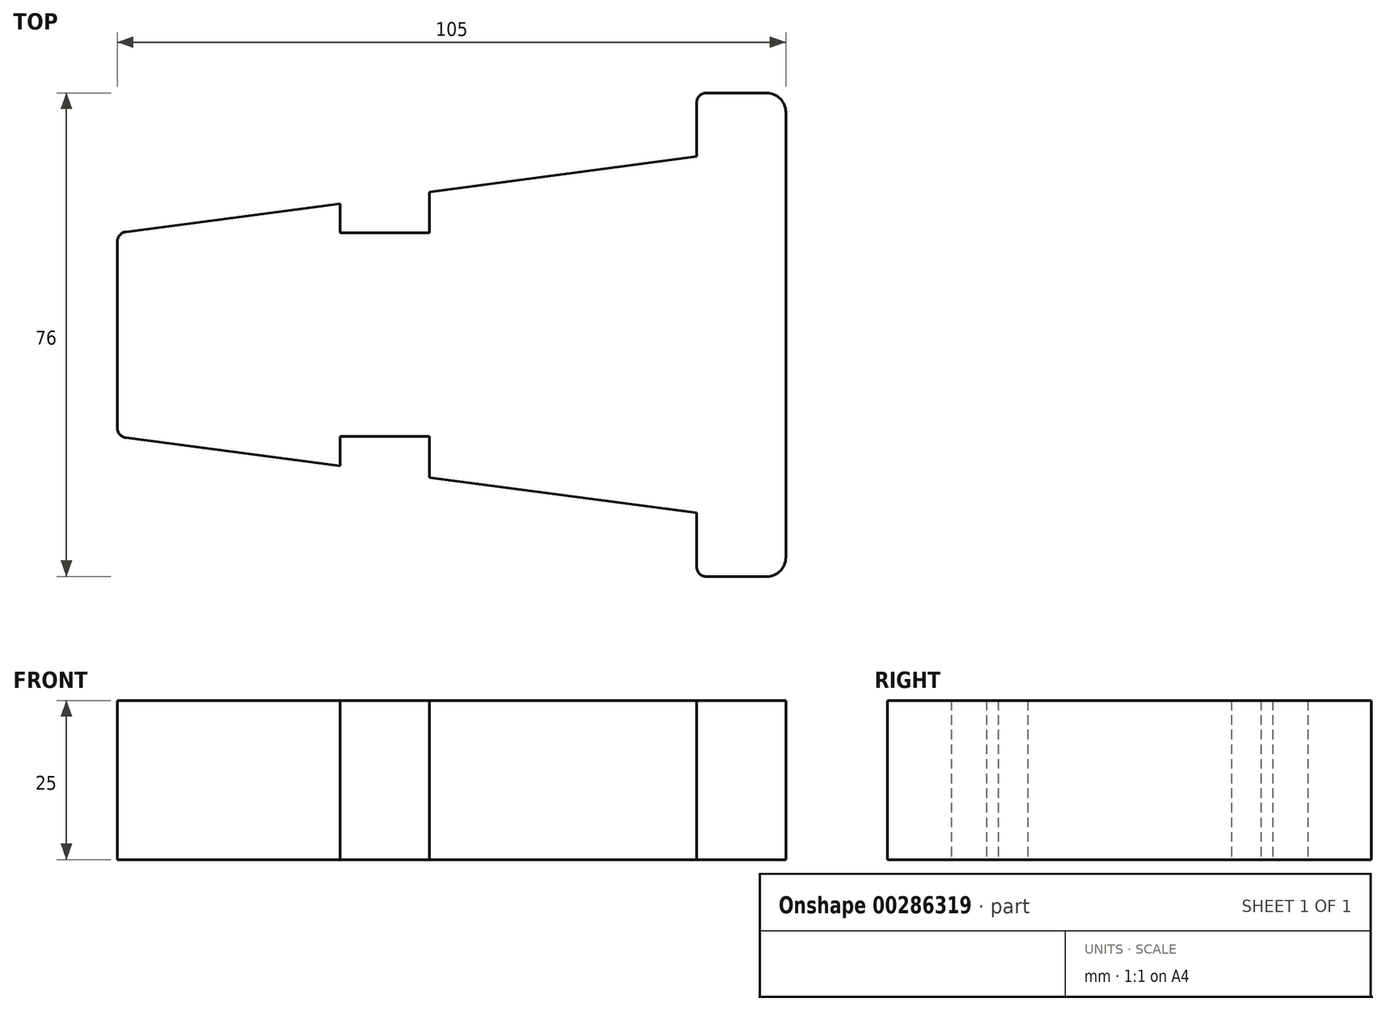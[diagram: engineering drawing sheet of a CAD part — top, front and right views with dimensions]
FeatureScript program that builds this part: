
annotation { "Feature Type Name" : "Feature", "Feature Type Description" : "" }
export const myFeature = defineFeature(function(context is Context, id is Id, definition is map)
    precondition{}
    {
        {
            var Q0;
            Q0=qCreatedBy(makeId("Top.planeOp"),FACE);
            var sketch = newSketch(context, id + "F0", { "sketchPlane" : qUnion([Q0])});
            skLineSegment(sketch, "E0", {"start": v(92.5, 51.46) * mm, "end": v(102, 51.46) * mm});
            skLineSegment(sketch, "E1", {"start": v(105, 48.46) * mm, "end": v(105, -21.54) * mm});
            skLineSegment(sketch, "E2", {"start": v(102, -24.54) * mm, "end": v(92.5, -24.54) * mm});
            skLineSegment(sketch, "E3", {"start": v(91, -23.04) * mm, "end": v(91, -14.54) * mm});
            skLineSegment(sketch, "E4", {"start": v(91, 49.96) * mm, "end": v(91, 41.46) * mm});
            skLineSegment(sketch, "E5", {"start": v(1.3, -2.71) * mm, "end": v(35, -7.16) * mm});
            skLineSegment(sketch, "E6", {"start": v(1.3, 29.63) * mm, "end": v(35, 34.07) * mm});
            skLineSegment(sketch, "E7", {"start": v(35, -7.16) * mm, "end": v(35, -2.54) * mm});
            skLineSegment(sketch, "E8", {"start": v(49, -2.54) * mm, "end": v(35, -2.54) * mm});
            skLineSegment(sketch, "E9", {"start": v(49, -2.54) * mm, "end": v(49, -9) * mm});
            skLineSegment(sketch, "E10", {"start": v(35, 29.46) * mm, "end": v(35, 34.07) * mm});
            skLineSegment(sketch, "E11", {"start": v(35, 29.46) * mm, "end": v(49, 29.46) * mm});
            skLineSegment(sketch, "E12", {"start": v(49, 29.46) * mm, "end": v(49, 35.92) * mm});
            skLineSegment(sketch, "E13.trimOffspring", {"start": v(49, 35.92) * mm, "end": v(91, 41.46) * mm});
            skLineSegment(sketch, "E14.trimOffspring", {"start": v(49, -9) * mm, "end": v(91, -14.54) * mm});
            skPoint(sketch, "E15.visualSharp", {"position": v(0, 29.46) * mm});
            skArc(sketch, "E15.filletArc", {"start": v(1.3, 29.63) * mm, "mid": v(0.37, 29.13) * mm, "end": v(0, 28.14) * mm});
            skPoint(sketch, "E16.visualSharp", {"position": v(0, -2.54) * mm});
            skArc(sketch, "E16.filletArc", {"start": v(0, -1.23) * mm, "mid": v(0.37, -2.22) * mm, "end": v(1.3, -2.71) * mm});
            skPoint(sketch, "E17.visualSharp", {"position": v(105, 51.46) * mm});
            skArc(sketch, "E17.filletArc", {"start": v(105, 48.46) * mm, "mid": v(104.12, 50.58) * mm, "end": v(102, 51.46) * mm});
            skPoint(sketch, "E18.visualSharp", {"position": v(105, -24.54) * mm});
            skArc(sketch, "E18.filletArc", {"start": v(102, -24.54) * mm, "mid": v(104.12, -23.66) * mm, "end": v(105, -21.54) * mm});
            skPoint(sketch, "E19.visualSharp", {"position": v(91, 51.46) * mm});
            skArc(sketch, "E19.filletArc", {"start": v(92.5, 51.46) * mm, "mid": v(91.44, 51.02) * mm, "end": v(91, 49.96) * mm});
            skPoint(sketch, "E20.visualSharp", {"position": v(91, -24.54) * mm});
            skArc(sketch, "E20.filletArc", {"start": v(91, -23.04) * mm, "mid": v(91.44, -24.1) * mm, "end": v(92.5, -24.54) * mm});
            skLineSegment(sketch, "E21", {"start": v(0, 28.14) * mm, "end": v(0, -1.23) * mm});
            skSolve(sketch);
        }
        {
            var Q0;
            Q0 = qSketchRegion(id + "F0", true);
            extrude(context, id + "F1", {"entities" : qUnion([Q0]), "depth" : 25 * mm});
        }
    });
